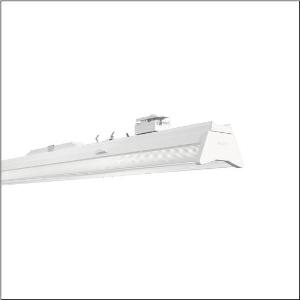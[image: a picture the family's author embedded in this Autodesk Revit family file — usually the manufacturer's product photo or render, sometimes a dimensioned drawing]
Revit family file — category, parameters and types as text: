
# Revit family: licross_r__21_performance_ho_52tm16cn4c5m_51b1
name_source: partatom
category: Lighting Fixtures
units: mm (PartAtom-declared; Revit-internal decimal feet)

## family parameters
Cut with Voids When Loaded = No
Host = Face
Light Source = No
Part Type = Normal
Room Calculation Point = No
Round Connector Dimension = Use Diameter
Shared = No

## types (1)
- --- (1 x LED, 12610 lm, 68.9 W, 4000K)
    Apparent Load = 69 VA
    CIE Flux Codes = 63 87 95 78 100
    Color Rendering = 80
    Color Temperature = 4000K
    Default Elevation = 1800 mm
    Description = Licross® 21 Performance HO, luminaire insert, of sheet steel, galvanised, coil coated, white, length: 1.500mm, width: 120mm, height: 123mm, LED rated luminous flux: 12.610lm, light colour: 840, control gear: ON/OFF Multilumen, CLOi, control gear: ECG Multilumen, with plug, 3-pole, with phase selection, mains connection: 220..240V, AC, 50/60Hz, start of lifetime: 69W, end of service life: 83W, halogen-free wiring, primary light control with lens, of plastic, primary optical cover: cover, of PMMA, light emission: direct/indirect distribution, primary light characteristic: symmetric, protection rating (complete): IP40, insulation class (complete): insulation class I (protective earthing), certification: CE, ENEC, UKCA, protection symbol: D if used in an environment without relevant dust loads with corresponding accessories, impact resistance: IK06, permissible ambient temperature for indoor applications: -35..+35°C, corresponds to IFS (International Featured Standards) requirements for safety and quality in the food industry, reducing of maximum allowable ambient temperature of 5°C with ceiling mounting, LABS conformity tested according to VDMA 24364:2018-05, packaging unit: 1 piece
    Height = 114 mm
    Lamp = 1 x LED
    Lamp Light Flux = 12610 lm
    Lamp Power = 68.9 W
    Lamp count = 1
    Length = 1500 mm
    Luminous efficacy = 183 lm/W
    Manufacturer = Siteco
    ModVariant = No
    Model = 52TM16CN4C5M
    Mounting Place = Ceiling
    Mounting Type = Pendant
    Number of Poles = 1
    OnlyDefault = Yes
    Power Factor = 1
    Product Name = Licross® 21 Performance HO
    Product group = luminaire insert
    ProductGroupID = 901
    Protection Class = Protection class I
    Protection Degree = IP 40
    RLX_Detail_Level = 1
    RLX_Emergency_Light_Flux = 0 lm
    RLX_Emergency_Type = 0
    RLX_Emergency_Type_DB = No
    RlxData = <blob elided: 31809 chars, md5=5b2bbb5b>
    Socket = socket
    Standby Power = 0 W
    System Light Flux = 12610 lm
    System Power = 69 W
    Type Comments = factory setting: luminous flux: 100 % | (A | C | E) | 162 mA
    Type Image = l_1256138.jpg
    URL = http://relux.com
    VarID = @adj_041713
    Voltage = 0 V
    Weight = 0.00 kg
    Width = 120 mm

## geometry (parser evidence)
native form markers: Blend x4, Sweep x11
no freeform markers — native parametric forms only
